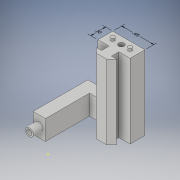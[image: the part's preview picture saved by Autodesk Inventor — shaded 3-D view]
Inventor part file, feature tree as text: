
AUTODESK INVENTOR PART (.ipt)
format: ipt  version: 2018 (Build 220112000, 112)  size: 187,904 bytes
history: native  units: in
note: dims shown in document units (in); Inventor stores cm internally (conversion verified against a paired STEP export)
features: sketch x10, extrude x7, other x3, hole x2
ambient origin geometry x8: Origin, YZ Plane, XZ Plane, XY Plane, X Axis, Y Axis, Z Axis, Center Point
bodies: Solid1 (feature_tree)
feature tree (22):
  other  "Annotations"
  extrude  "Extrusion1"  Depth=0.3in
  extrude  "Extrusion2"  Depth=0.25in
  extrude  "Extrusion3"  Depth=0.05in
  hole  "Hole1"  [1 undecoded]
  extrude  "Extrusion7"  Depth=0.1in
  extrude  "Extrusion8"  Depth=0.15in
  extrude  "Extrusion9"  Depth=0.05in TaperAngle=0.0deg
  sketch  "Sketch16"  dims[d20=0.15in d21=0.08in]
  hole  "Hole3"  [1 undecoded]
  extrude  "Extrusion10"  Depth=0.05in
  sketch  "Sketch1"  dims[d0=0.65in d1=0.3in]
  sketch  "Sketch2"  dims[d2=0.1in d3=0.25in]
  sketch  "Sketch3"  dims[d4=0.2in d5=0.05in]
  sketch  "Sketch6"  dims[d6=0.1in d7=0.1in]
  sketch  "Sketch13"  dims[d8=0.1in d9=0.1in]
  sketch  "Sketch14"  dims[d10=1.5in d11=0.0in d12=0.15in]
  sketch  "Sketch15"  dims[d14=0.08in d18=0.05in d19=0.0in]
  sketch  "Sketch17"  dims[d22=0.05in d23=0.0in d24=0.325in]
  sketch  "Sketch18"  dims[d25=0.11in d26=0.11in d27=0.75in d28=0.375in d29=0.25in d30=0.5635in d31=0.45in d32=0.8108in d68=0.22in d69=0.4in d70=0.5in d71=0.0in d72=0.25in d73=0.4in d77=0.89in d78=0.0in d79=0.125in d80=0.16in d81=0.2in d82=0.0in d83=0.11in d84=0.11in d85=0.75in d86=0.375in d87=0.25in d88=0.5635in d89=0.5in d90=0.8108in d94=0.05in d95=0.0in d91=0.0911in d92=0.1714in d93=0.65in d96=0.2651in d97=0.318in d98=0.3in]
  other  "Linear Dimension 1"
  other  "Linear Dimension 2"
note: 2 required parameter values undecoded (feature->parameter linkage not recoverable at this tier; creation-order binding heuristic only, values carry confidence <= 0.55)
